# Revit family: Hydrant_Yard-Zurn-Z1397XL-Lead_Free
name_source: partatom
category: Plumbing Fixtures
units: mm (PartAtom-declared; Revit-internal decimal feet)

## family parameters
Cut with Voids When Loaded = No
Host = Face
Maintain Annotation Orientation = No
OmniClass Number = 23.65.70.14.11
OmniClass Title = Drinking Fountains/Coolers
Part Type = Normal
Room Calculation Point = No
Round Connector Dimension = Use Radius
Shared = No

## types (6) — shared parameters
Assembly Code = D2020300
CW Connection = Yes
CWFU = 1
Casing Dia = 1.156 "
Default Elevation = 20 "
Description = FLO-TROL YARD HYDRANT Exposed Head, Non-Freeze
Female NPT Inlet Radius (Inner) = 0.41 "
Female NPT Inlet Radius (Nominal) = 0.375 "
Female NPT Inlet Radius (Outer) = 0.525 "
HW Connection = No
Hose Outlet Radius (Inner) = 0.41 "
Hose Outlet Radius (Nominal) = 0.375 "
Hose Outlet Radius (Outer) = 0.525 "
Hose and Valve Housing = Bronze - Zurn - Cast
Hydrant Casing = Steel - Zurn - Galvanized
Manufacturer = Zurn Water, LLC
Manufacturer Brand = Zurn
Model = Z1397XL
Modified Date = 03/02/2026
Product Documentation Link = https://files.zurn.com
Product Page URL = https://www.zurn.com
Product data url = https://www.bimobject.com
URL = www.zurn.com
Vent Connection = No
Waste Connection = No
zero-valued in all types: HWFU, WFU

## per-type parameters (varying)
| type | Approx.WT. | Depth of Bury | Height_B+ |
| Z1397XL-2 Foot Depth of Bury | 15.00 lb | 24 " | 54 " |
| Z1397XL-3 Foot Depth of Bury | 19.00 lb | 36 " | 66 " |
| Z1397XL-4 Foot Depth of Bury | 23.00 lb | 48 " | 78 " |
| Z1397XL-5 Foot Depth of Bury | 27.00 lb | 60 " | 90 " |
| Z1397XL-6 Foot Depth of Bury | 31.00 lb | 72 " | 102 " |
| Z1397XL-8 Foot Depth of Bury | 39.00 lb | 96 " | 126 " |

## geometry (parser evidence)
native form markers: Blend x8, Sweep x9
no freeform markers — native parametric forms only
